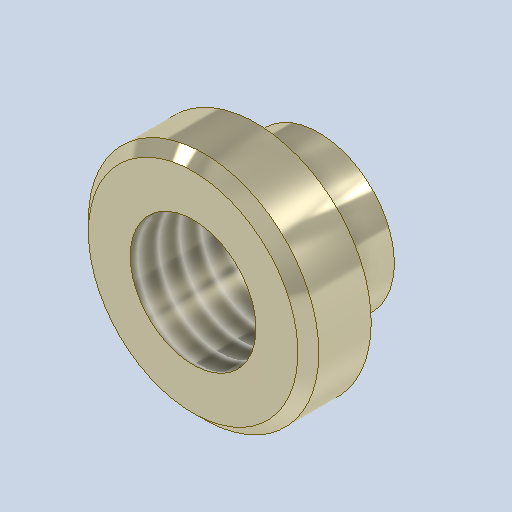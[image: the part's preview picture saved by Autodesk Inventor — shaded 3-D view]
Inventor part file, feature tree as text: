
AUTODESK INVENTOR PART (.ipt)
format: ipt  version: 2022 (Build 260153000, 153)  size: 164,352 bytes
history: native  units: mm
features: other x1, revolve x1, thread x1, chamfer x1, sketch x1
ambient origin geometry x8: Origin, YZ Plane, XZ Plane, XY Plane, X Axis, Y Axis, Z Axis, Center Point
bodies: Body1 (feature_tree)
feature tree (5):
  other  "Твердое тело1"
  revolve  "Вращение1"
  thread  "Резьба1"
  chamfer  "Фаска1"  Distance=2.75mm
  sketch  "Эскиз1"
